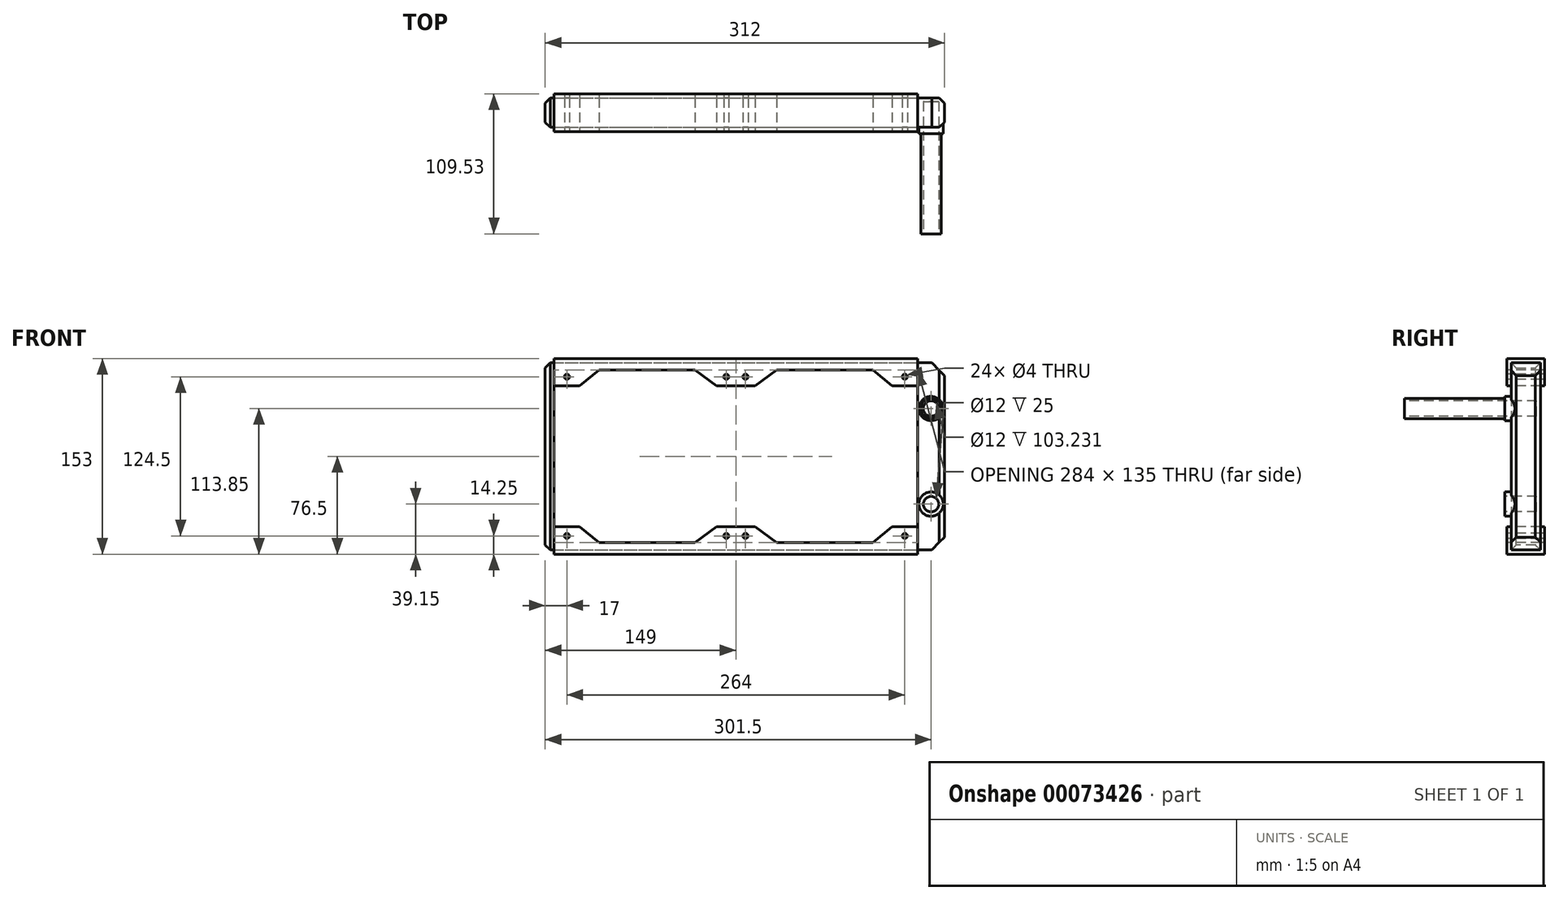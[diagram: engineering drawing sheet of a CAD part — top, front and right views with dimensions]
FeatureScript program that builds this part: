
annotation { "Feature Type Name" : "Feature", "Feature Type Description" : "" }
export const myFeature = defineFeature(function(context is Context, id is Id, definition is map)
    precondition{}
    {
        {
            var Q0;
            Q0=qCreatedBy(makeId("Front.planeOp"),FACE);
            var sketch = newSketch(context, id + "F0", { "sketchPlane" : qUnion([Q0])});
            skLineSegment(sketch, "E0.bottom", {"start": v(0, 73.2) * mm, "end": v(312, 73.2) * mm});
            skLineSegment(sketch, "E0.top", {"start": v(0, -73.2) * mm, "end": v(312, -73.2) * mm});
            skLineSegment(sketch, "E0.left", {"start": v(0, 73.2) * mm, "end": v(0, -73.2) * mm});
            skLineSegment(sketch, "E0.right", {"start": v(312, 73.2) * mm, "end": v(312, -73.2) * mm});
            skPoint(sketch, "E1", {"position": v(0, 0) * mm});
            skSolve(sketch);
        }
        {
            var Q0;
            Q0=qSketchRegion(id+"F0",true);
            extrude(context, id + "F1", {"entities" : qUnion([Q0]), "depth" : 23 * mm});
        }
        {
            var Q0;
            Q0=makeQuery(id+"F1.opExtrude","CAP_FACE",FACE,{"disambiguationData":[OSD([sQuery(id+"F0.wireOp",EDGE,"E0.bottom"),sQuery(id+"F0.wireOp",EDGE,"E0.top"),sQuery(id+"F0.wireOp",EDGE,"E0.left"),sQuery(id+"F0.wireOp",EDGE,"E0.right")])],"isStart":false});
            var sketch = newSketch(context, id + "F2", { "sketchPlane" : qUnion([Q0])});
            skCircle(sketch, "E2", {"center": v(301.5, 37.35) * mm, "radius": 9.5 * mm});
            skCircle(sketch, "E3", {"center": v(301.5, -37.35) * mm, "radius": 9.5 * mm});
            skLineSegment(sketch, "E4", {"start": v(312, 0) * mm, "end": v(0, 0) * mm, "construction": true});
            skSolve(sketch);
        }
        {
            var Q0;
            Q0=qSketchRegion(id+"F2",true);
            extrude(context, id + "F3", {"entities" : qUnion([Q0]), "operationType" : NewBodyOperationType.ADD, "depth" : 5 * mm});
        }
        {
            var Q0;
            Q0=makeQuery(id+"F3.opExtrude","CAP_FACE",FACE,{"disambiguationData":[OSD([sQuery(id+"F2.wireOp",EDGE,"E2")])],"isStart":false});
            var sketch = newSketch(context, id + "F4", { "sketchPlane" : qUnion([Q0])});
            skCircle(sketch, "E5", {"center": v(301.5, 37.35) * mm, "radius": 6 * mm});
            skCircle(sketch, "E6", {"center": v(301.5, -37.35) * mm, "radius": 6 * mm});
            skSolve(sketch);
        }
        {
            var Q0;
            Q0=qSketchRegion(id+"F4",true);
            extrude(context, id + "F5", {"entities" : qUnion([Q0]), "operationType" : NewBodyOperationType.REMOVE, "oppositeDirection" : true, "depth" : 25 * mm});
        }
        {
            var Q0;
            Q0=makeQuery(id+"F1.opExtrude","SWEPT_EDGE",EDGE,{"disambiguationData":[OSD([sQuery(id+"F0.wireOp",EDGE,"E0.top"),sQuery(id+"F0.wireOp",EDGE,"E0.right")])]});
            var Q1;
            Q1=makeQuery(id+"F1.opExtrude","SWEPT_EDGE",EDGE,{"disambiguationData":[OSD([sQuery(id+"F0.wireOp",EDGE,"E0.bottom"),sQuery(id+"F0.wireOp",EDGE,"E0.right")])]});
            chamfer(context, id + "F6", {"entities" : qUnion([Q0, Q1]), "width" : 10 * mm, "tangentPropagation" : true});
        }
        {
            var Q0;
            Q0=makeQuery(id+"F1.opExtrude","CAP_EDGE",EDGE,{"disambiguationData":[OSD([sQuery(id+"F0.wireOp",EDGE,"E0.right")])],"isStart":false});
            var Q1;
            Q1=makeQuery(id+"F1.opExtrude","CAP_EDGE",EDGE,{"disambiguationData":[OSD([sQuery(id+"F0.wireOp",EDGE,"E0.right")])],"isStart":true});
            var Q2;
            Q2=makeQuery(id+"F1.opExtrude","CAP_EDGE",EDGE,{"disambiguationData":[OSD([sQuery(id+"F0.wireOp",EDGE,"E0.left")])],"isStart":false});
            var Q3;
            Q3=makeQuery(id+"F1.opExtrude","CAP_EDGE",EDGE,{"disambiguationData":[OSD([sQuery(id+"F0.wireOp",EDGE,"E0.left")])],"isStart":true});
            var Q4;
            Q4=makeQuery(id+"F1.opExtrude","SWEPT_EDGE",EDGE,{"disambiguationData":[OSD([sQuery(id+"F0.wireOp",EDGE,"E0.top"),sQuery(id+"F0.wireOp",EDGE,"E0.left")])]});
            var Q5;
            Q5=makeQuery(id+"F1.opExtrude","SWEPT_EDGE",EDGE,{"disambiguationData":[OSD([sQuery(id+"F0.wireOp",EDGE,"E0.bottom"),sQuery(id+"F0.wireOp",EDGE,"E0.left")])]});
            chamfer(context, id + "F7", {"entities" : qUnion([Q0, Q1, Q2, Q3, Q4, Q5]), "width" : 4 * mm, "tangentPropagation" : true});
        }
        {
            var Q0;
            Q0=makeQuery(id+"F1.opExtrude","SWEPT_FACE",FACE,{"disambiguationData":[OSD([sQuery(id+"F0.wireOp",EDGE,"E0.left")])]});
            cPlane(context, id + "F8", {"entities" : qUnion([Q0]), "cplaneType" : CPlaneType.OFFSET, "offset" : 7 * mm, "oppositeDirection" : true, "width" : 150 * mm, "height" : 150 * mm});
        }
        {
            var Q0;
            Q0=qCreatedBy(id+"F8.planeOp",FACE);
            var sketch = newSketch(context, id + "F9", { "sketchPlane" : qUnion([Q0])});
            skLineSegment(sketch, "E7.bottom", {"start": v(-3.3, 76.5) * mm, "end": v(26.3, 76.5) * mm});
            skLineSegment(sketch, "E7.top", {"start": v(-3.3, -76.5) * mm, "end": v(26.3, -76.5) * mm});
            skLineSegment(sketch, "E7.left", {"start": v(-3.3, 76.5) * mm, "end": v(-3.3, -76.5) * mm});
            skLineSegment(sketch, "E7.right", {"start": v(26.3, 76.5) * mm, "end": v(26.3, -76.5) * mm});
            skLineSegment(sketch, "E8", {"start": v(0, 0) * mm, "end": v(-3.3, 0) * mm, "construction": true});
            skLineSegment(sketch, "E9.bottom", {"start": v(0, 73.2) * mm, "end": v(23, 73.2) * mm});
            skLineSegment(sketch, "E9.top", {"start": v(0, -73.2) * mm, "end": v(23, -73.2) * mm});
            skLineSegment(sketch, "E9.left", {"start": v(0, 73.2) * mm, "end": v(0, -73.2) * mm});
            skLineSegment(sketch, "E9.right", {"start": v(23, 73.2) * mm, "end": v(23, -73.2) * mm});
            skSolve(sketch);
        }
        {
            var Q0;
            Q0=qSketchRegion(id+"F9",true);
            extrude(context, id + "F10", {"entities" : qUnion([Q0]), "oppositeDirection" : true, "depth" : 284 * mm});
        }
        {
            var Q0;
            Q0=makeQuery(id+"F10.opExtrude","SWEPT_FACE",FACE,{"disambiguationData":[OSD([sQuery(id+"F9.wireOp",EDGE,"E7.right")])]});
            var sketch = newSketch(context, id + "F11", { "sketchPlane" : qUnion([Q0])});
            skCircle(sketch, "E10", {"center": v(17, 62.25) * mm, "radius": 2 * mm});
            skCircle(sketch, "E11", {"center": v(141.5, 62.25) * mm, "radius": 2 * mm});
            skCircle(sketch, "E12", {"center": v(156.5, 62.25) * mm, "radius": 2 * mm});
            skCircle(sketch, "E13", {"center": v(281, 62.25) * mm, "radius": 2 * mm});
            skLineSegment(sketch, "E14", {"start": v(7, 0) * mm, "end": v(291, 0) * mm, "construction": true});
            skLineSegment(sketch, "E15", {"start": v(149, 76.5) * mm, "end": v(149, -76.5) * mm, "construction": true});
            skCircle(sketch, "E16.MirrorC", {"center": v(17, -62.25) * mm, "radius": 2 * mm});
            skCircle(sketch, "E17.MirrorC", {"center": v(141.5, -62.25) * mm, "radius": 2 * mm});
            skCircle(sketch, "E18.MirrorC", {"center": v(156.5, -62.25) * mm, "radius": 2 * mm});
            skCircle(sketch, "E19.MirrorC", {"center": v(281, -62.25) * mm, "radius": 2 * mm});
            skSolve(sketch);
        }
        {
            var Q0;
            Q0=qSketchRegion(id+"F11",true);
            extrude(context, id + "F12", {"entities" : qUnion([Q0]), "operationType" : NewBodyOperationType.REMOVE, "endBound" : BoundingType.THROUGH_ALL, "oppositeDirection" : true, "depth" : 25 * mm});
        }
        {
            var Q0;
            Q0=makeQuery(id+"F10.opExtrude","SWEPT_FACE",FACE,{"disambiguationData":[OSD([sQuery(id+"F9.wireOp",EDGE,"E7.right")])]});
            var sketch = newSketch(context, id + "F13", { "sketchPlane" : qUnion([Q0])});
            skLineSegment(sketch, "E20", {"start": v(7, 55) * mm, "end": v(27, 55) * mm});
            skLineSegment(sketch, "E21", {"start": v(27, 55) * mm, "end": v(42, 67.5) * mm});
            skLineSegment(sketch, "E22", {"start": v(42, 67.5) * mm, "end": v(117, 67.5) * mm});
            skLineSegment(sketch, "E23", {"start": v(117, 67.5) * mm, "end": v(134, 55) * mm});
            skLineSegment(sketch, "E24", {"start": v(134, 55) * mm, "end": v(164, 55) * mm});
            skLineSegment(sketch, "E25", {"start": v(164, 55) * mm, "end": v(181, 67.5) * mm});
            skLineSegment(sketch, "E26", {"start": v(181, 67.5) * mm, "end": v(256, 67.5) * mm});
            skLineSegment(sketch, "E27", {"start": v(256, 67.5) * mm, "end": v(271, 55) * mm});
            skLineSegment(sketch, "E28", {"start": v(271, 55) * mm, "end": v(291, 55) * mm});
            skLineSegment(sketch, "E29", {"start": v(291, 55) * mm, "end": v(291, 0) * mm});
            skLineSegment(sketch, "E30", {"start": v(7, 55) * mm, "end": v(7, 0) * mm});
            skLineSegment(sketch, "E31", {"start": v(7, 0) * mm, "end": v(291, 0) * mm, "construction": true});
            skLineSegment(sketch, "E32", {"start": v(149, 76.5) * mm, "end": v(149, 55) * mm, "construction": true});
            skLineSegment(sketch, "E33.MirrorCS", {"start": v(291, -55) * mm, "end": v(291, 0) * mm});
            skLineSegment(sketch, "E34.MirrorCS", {"start": v(271, -55) * mm, "end": v(291, -55) * mm});
            skLineSegment(sketch, "E35.MirrorCS", {"start": v(256, -67.5) * mm, "end": v(271, -55) * mm});
            skLineSegment(sketch, "E36.MirrorCS", {"start": v(181, -67.5) * mm, "end": v(256, -67.5) * mm});
            skLineSegment(sketch, "E37.MirrorCS", {"start": v(164, -55) * mm, "end": v(181, -67.5) * mm});
            skLineSegment(sketch, "E38.MirrorCS", {"start": v(134, -55) * mm, "end": v(164, -55) * mm});
            skLineSegment(sketch, "E39.MirrorCS", {"start": v(117, -67.5) * mm, "end": v(134, -55) * mm});
            skLineSegment(sketch, "E40.MirrorCS", {"start": v(42, -67.5) * mm, "end": v(117, -67.5) * mm});
            skLineSegment(sketch, "E41.MirrorCS", {"start": v(27, -55) * mm, "end": v(42, -67.5) * mm});
            skLineSegment(sketch, "E42.MirrorCS", {"start": v(7, -55) * mm, "end": v(7, 0) * mm});
            skLineSegment(sketch, "E43.MirrorCS", {"start": v(7, -55) * mm, "end": v(27, -55) * mm});
            skSolve(sketch);
        }
        {
            var Q0;
            Q0=qSketchRegion(id+"F13",true);
            extrude(context, id + "F14", {"entities" : qUnion([Q0]), "operationType" : NewBodyOperationType.REMOVE, "endBound" : BoundingType.THROUGH_ALL, "oppositeDirection" : true, "depth" : 25 * mm});
        }
        {
            var Q0;
            Q0=makeQuery(id+"F3.opExtrude","CAP_FACE",FACE,{"disambiguationData":[OSD([sQuery(id+"F2.wireOp",EDGE,"E2")])],"isStart":false});
            var sketch = newSketch(context, id + "F15", { "sketchPlane" : qUnion([Q0])});
            skCircle(sketch, "E44", {"center": v(301.5, 37.35) * mm, "radius": 8 * mm});
            skCircle(sketch, "E45", {"center": v(301.5, 37.35) * mm, "radius": 6 * mm});
            skSolve(sketch);
        }
        {
            var Q0;
            Q0 = qSketchRegion(id + "F15", true);
            extrude(context, id + "F16", {"entities" : qUnion([Q0]), "operationType" : NewBodyOperationType.ADD, "depth" : 78.23 * mm});
        }
    });
